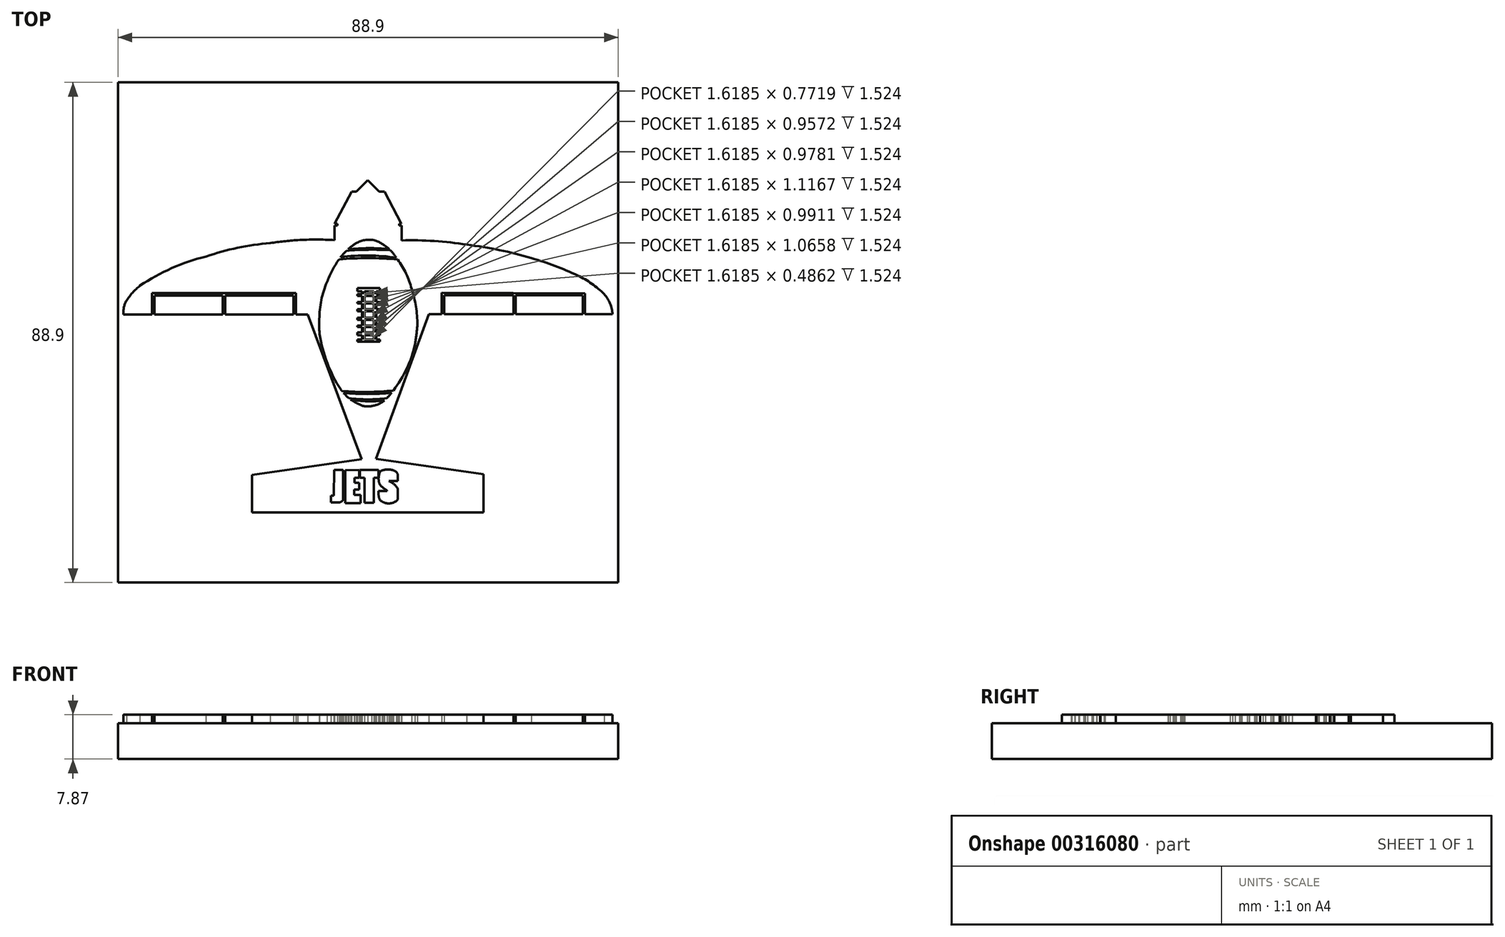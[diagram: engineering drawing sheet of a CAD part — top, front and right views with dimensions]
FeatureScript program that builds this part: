
annotation { "Feature Type Name" : "Feature", "Feature Type Description" : "" }
export const myFeature = defineFeature(function(context is Context, id is Id, definition is map)
    precondition{}
    {
        {
            var Q0;
            Q0=qCreatedBy(makeId("Top.planeOp"),FACE);
            var sketch = newSketch(context, id + "F0", { "sketchPlane" : qUnion([Q0])});
            skLineSegment(sketch, "E0.bottom", {"start": v(0, 0) * mm, "end": v(88.9, 0) * mm});
            skLineSegment(sketch, "E0.top", {"start": v(0, 88.9) * mm, "end": v(88.9, 88.9) * mm});
            skLineSegment(sketch, "E0.left", {"start": v(0, 0) * mm, "end": v(0, 88.9) * mm});
            skLineSegment(sketch, "E0.right", {"start": v(88.9, 0) * mm, "end": v(88.9, 88.9) * mm});
            skSolve(sketch);
        }
        {
            var Q0;
            Q0=makeQuery(id+"F0.imprint","IMPRINT",FACE,{"disambiguationData":[TD([[makeQuery(id+"F0.imprint","IMPRINT",EDGE,{"derivedFrom":sQuery(id+"F0.wireOp",EDGE,"E0.bottom")}),1.0]])]});
            extrude(context, id + "F1", {"entities" : qUnion([Q0]), "depth" : 6.35 * mm});
        }
        {
            var Q0;
            Q0=makeQuery(id+"F1.opExtrude","CAP_FACE",FACE,{"disambiguationData":[OSD([sQuery(id+"F0.wireOp",EDGE,"E0.bottom"),sQuery(id+"F0.wireOp",EDGE,"E0.top"),sQuery(id+"F0.wireOp",EDGE,"E0.left"),sQuery(id+"F0.wireOp",EDGE,"E0.right")])],"isStart":false});
            var sketch = newSketch(context, id + "F2", { "sketchPlane" : qUnion([Q0])});
            skLineSegment(sketch, "E1", {"start": v(43.29, 21.93) * mm, "end": v(23.83, 19.13) * mm});
            skLineSegment(sketch, "E2", {"start": v(23.83, 19.13) * mm, "end": v(23.83, 12.44) * mm});
            skLineSegment(sketch, "E3", {"start": v(23.83, 12.44) * mm, "end": v(64.97, 12.44) * mm});
            skLineSegment(sketch, "E4", {"start": v(64.97, 12.44) * mm, "end": v(64.97, 19.23) * mm});
            skLineSegment(sketch, "E5", {"start": v(64.97, 19.23) * mm, "end": v(45.85, 22) * mm});
            skLineSegment(sketch, "E6", {"start": v(45.85, 22) * mm, "end": v(55.28, 47.7) * mm});
            skLineSegment(sketch, "E7", {"start": v(55.28, 47.7) * mm, "end": v(87.89, 47.7) * mm});
            skLineSegment(sketch, "E8", {"start": v(43.29, 21.93) * mm, "end": v(33.7, 47.66) * mm});
            skLineSegment(sketch, "E9", {"start": v(33.7, 47.66) * mm, "end": v(0.98, 47.66) * mm});
            skArc(sketch, "E10", {"start": v(1.51, 50.1) * mm, "mid": v(1.05, 48.92) * mm, "end": v(0.98, 47.66) * mm});
            skArc(sketch, "E11", {"start": v(3.9, 52.77) * mm, "mid": v(2.6, 51.54) * mm, "end": v(1.51, 50.1) * mm});
            skArc(sketch, "E12", {"start": v(15.62, 57.96) * mm, "mid": v(9.54, 55.87) * mm, "end": v(3.9, 52.77) * mm});
            skArc(sketch, "E13", {"start": v(27.06, 60.35) * mm, "mid": v(21.27, 59.5) * mm, "end": v(15.62, 57.96) * mm});
            skArc(sketch, "E14", {"start": v(31.92, 60.89) * mm, "mid": v(29.49, 60.65) * mm, "end": v(27.06, 60.35) * mm});
            skArc(sketch, "E15", {"start": v(38.5, 60.89) * mm, "mid": v(35.22, 60.96) * mm, "end": v(31.92, 60.89) * mm});
            skLineSegment(sketch, "E16", {"start": v(38.5, 60.89) * mm, "end": v(38.5, 63.8) * mm});
            skLineSegment(sketch, "E17", {"start": v(38.5, 63.8) * mm, "end": v(41.53, 69.51) * mm});
            skLineSegment(sketch, "E18", {"start": v(41.53, 69.51) * mm, "end": v(42.36, 69.51) * mm});
            skLineSegment(sketch, "E19", {"start": v(42.36, 69.51) * mm, "end": v(44.4, 71.55) * mm});
            skLineSegment(sketch, "E20", {"start": v(44.4, 71.55) * mm, "end": v(46.45, 69.51) * mm});
            skLineSegment(sketch, "E21", {"start": v(46.45, 69.51) * mm, "end": v(47.36, 69.51) * mm});
            skLineSegment(sketch, "E22", {"start": v(47.36, 69.51) * mm, "end": v(50.4, 63.73) * mm});
            skLineSegment(sketch, "E23", {"start": v(50.4, 63.73) * mm, "end": v(50.4, 60.81) * mm});
            skArc(sketch, "E24", {"start": v(62.01, 60.06) * mm, "mid": v(56.22, 60.7) * mm, "end": v(50.4, 60.81) * mm});
            skArc(sketch, "E25", {"start": v(73.5, 57.67) * mm, "mid": v(67.8, 59.1) * mm, "end": v(62.01, 60.06) * mm});
            skArc(sketch, "E26", {"start": v(81.72, 54.57) * mm, "mid": v(77.67, 56.3) * mm, "end": v(73.5, 57.67) * mm});
            skArc(sketch, "E27", {"start": v(86.42, 51.26) * mm, "mid": v(84.22, 53.12) * mm, "end": v(81.72, 54.57) * mm});
            skArc(sketch, "E28", {"start": v(87.89, 47.7) * mm, "mid": v(87.47, 49.6) * mm, "end": v(86.42, 51.26) * mm});
            skLineSegment(sketch, "E29", {"start": v(6.04, 47.66) * mm, "end": v(6.04, 51.44) * mm});
            skLineSegment(sketch, "E30", {"start": v(6.04, 51.44) * mm, "end": v(31.62, 51.44) * mm});
            skLineSegment(sketch, "E31", {"start": v(31.62, 51.44) * mm, "end": v(31.62, 47.66) * mm});
            skLineSegment(sketch, "E32", {"start": v(31.19, 47.66) * mm, "end": v(31.19, 51.44) * mm});
            skLineSegment(sketch, "E33", {"start": v(19.05, 51.44) * mm, "end": v(19.05, 47.66) * mm});
            skLineSegment(sketch, "E34", {"start": v(18.64, 51.44) * mm, "end": v(18.64, 47.66) * mm});
            skLineSegment(sketch, "E35", {"start": v(6.47, 51.44) * mm, "end": v(6.47, 47.66) * mm});
            skLineSegment(sketch, "E36", {"start": v(57.57, 47.7) * mm, "end": v(57.57, 51.55) * mm});
            skLineSegment(sketch, "E37", {"start": v(57.57, 51.55) * mm, "end": v(82.99, 51.42) * mm});
            skLineSegment(sketch, "E38", {"start": v(82.99, 51.42) * mm, "end": v(82.99, 47.7) * mm});
            skLineSegment(sketch, "E39", {"start": v(70.28, 51.49) * mm, "end": v(70.28, 48.09) * mm});
            skLineSegment(sketch, "E40", {"start": v(70.66, 51.48) * mm, "end": v(70.66, 48.09) * mm});
            skArc(sketch, "E41", {"start": v(35.79, 46.83) * mm, "mid": v(35.76, 45.5) * mm, "end": v(35.85, 44.18) * mm});
            skArc(sketch, "E42", {"start": v(37.16, 53.42) * mm, "mid": v(36.14, 50.2) * mm, "end": v(35.79, 46.83) * mm});
            skArc(sketch, "E43", {"start": v(39.56, 57.83) * mm, "mid": v(38.21, 55.7) * mm, "end": v(37.16, 53.42) * mm});
            skArc(sketch, "E44", {"start": v(42.46, 60.4) * mm, "mid": v(40.9, 59.24) * mm, "end": v(39.56, 57.83) * mm});
            skArc(sketch, "E45", {"start": v(45.73, 60.82) * mm, "mid": v(44.06, 60.9) * mm, "end": v(42.46, 60.4) * mm});
            skArc(sketch, "E46", {"start": v(49.5, 57.73) * mm, "mid": v(47.85, 59.56) * mm, "end": v(45.73, 60.82) * mm});
            skArc(sketch, "E47", {"start": v(52.2, 52.2) * mm, "mid": v(51.12, 55.09) * mm, "end": v(49.5, 57.73) * mm});
            skArc(sketch, "E48", {"start": v(53.22, 45.8) * mm, "mid": v(52.96, 49.03) * mm, "end": v(52.2, 52.2) * mm});
            skArc(sketch, "E49", {"start": v(52.8, 42.33) * mm, "mid": v(53.04, 44.06) * mm, "end": v(53.22, 45.8) * mm});
            skArc(sketch, "E50", {"start": v(48.2, 59.26) * mm, "mid": v(44.55, 59.44) * mm, "end": v(40.9, 59.24) * mm});
            skArc(sketch, "E51", {"start": v(48.39, 59.08) * mm, "mid": v(44.5, 59.17) * mm, "end": v(40.6, 58.98) * mm});
            skArc(sketch, "E52", {"start": v(49.5, 57.73) * mm, "mid": v(44.53, 58.14) * mm, "end": v(39.56, 57.83) * mm});
            skArc(sketch, "E53", {"start": v(49.71, 57.43) * mm, "mid": v(44.5, 57.67) * mm, "end": v(39.28, 57.45) * mm});
            skArc(sketch, "E54", {"start": v(35.85, 44.18) * mm, "mid": v(37.2, 39.04) * mm, "end": v(39.6, 34.3) * mm});
            skArc(sketch, "E55", {"start": v(39.6, 34.3) * mm, "mid": v(41.06, 32.78) * mm, "end": v(42.87, 31.7) * mm});
            skArc(sketch, "E56", {"start": v(42.87, 31.7) * mm, "mid": v(43.95, 31.33) * mm, "end": v(45.09, 31.37) * mm});
            skArc(sketch, "E57", {"start": v(45.09, 31.37) * mm, "mid": v(46.46, 31.8) * mm, "end": v(47.65, 32.61) * mm});
            skArc(sketch, "E58", {"start": v(47.65, 32.61) * mm, "mid": v(50.87, 37.13) * mm, "end": v(52.8, 42.33) * mm});
            skArc(sketch, "E59", {"start": v(39.8, 34.06) * mm, "mid": v(44.38, 33.88) * mm, "end": v(48.96, 34.15) * mm});
            skArc(sketch, "E60", {"start": v(40.09, 33.7) * mm, "mid": v(44.35, 33.52) * mm, "end": v(48.62, 33.72) * mm});
            skArc(sketch, "E61", {"start": v(41.06, 32.78) * mm, "mid": v(44.44, 32.56) * mm, "end": v(47.81, 32.78) * mm});
            skPoint(sketch, "E61.endSnap0", {"position": v(41.06, 32.78) * mm});
            skArc(sketch, "E62", {"start": v(41.35, 32.56) * mm, "mid": v(44.35, 32.22) * mm, "end": v(47.37, 32.37) * mm});
            skLineSegment(sketch, "E63", {"start": v(38.5, 63.8) * mm, "end": v(50.36, 63.8) * mm});
            skLineSegment(sketch, "E64", {"start": v(40.04, 19.93) * mm, "end": v(40.04, 14.74) * mm});
            skArc(sketch, "E65", {"start": v(39.33, 14.24) * mm, "mid": v(39.75, 14.4) * mm, "end": v(40.04, 14.74) * mm});
            skLineSegment(sketch, "E66", {"start": v(39.33, 14.24) * mm, "end": v(37.84, 14.24) * mm});
            skLineSegment(sketch, "E67", {"start": v(37.84, 14.24) * mm, "end": v(37.84, 15.43) * mm});
            skLineSegment(sketch, "E68", {"start": v(37.84, 15.43) * mm, "end": v(38.39, 15.43) * mm});
            skLineSegment(sketch, "E69", {"start": v(38.39, 15.43) * mm, "end": v(38.46, 20.02) * mm});
            skLineSegment(sketch, "E70", {"start": v(38.46, 20.02) * mm, "end": v(40.04, 20.02) * mm});
            skLineSegment(sketch, "E71", {"start": v(40.04, 20.02) * mm, "end": v(40.04, 19.93) * mm});
            skLineSegment(sketch, "E72", {"start": v(40.36, 19.97) * mm, "end": v(40.36, 14.14) * mm});
            skLineSegment(sketch, "E73", {"start": v(40.36, 14.14) * mm, "end": v(43.13, 14.14) * mm});
            skLineSegment(sketch, "E74", {"start": v(43.13, 14.14) * mm, "end": v(43.13, 15.57) * mm});
            skLineSegment(sketch, "E75", {"start": v(43.13, 15.57) * mm, "end": v(42, 15.57) * mm});
            skLineSegment(sketch, "E76", {"start": v(42, 15.57) * mm, "end": v(42, 16.53) * mm});
            skLineSegment(sketch, "E77", {"start": v(42, 16.53) * mm, "end": v(42.86, 16.53) * mm});
            skLineSegment(sketch, "E78", {"start": v(42.86, 16.53) * mm, "end": v(42.86, 17.77) * mm});
            skLineSegment(sketch, "E79", {"start": v(42.86, 17.77) * mm, "end": v(42.04, 17.77) * mm});
            skLineSegment(sketch, "E80", {"start": v(42.04, 17.77) * mm, "end": v(42.04, 18.63) * mm});
            skLineSegment(sketch, "E81", {"start": v(42.04, 18.63) * mm, "end": v(42.86, 18.63) * mm});
            skLineSegment(sketch, "E82", {"start": v(42.86, 18.63) * mm, "end": v(42.86, 20.02) * mm});
            skLineSegment(sketch, "E83", {"start": v(42.86, 20.02) * mm, "end": v(40.36, 19.97) * mm});
            skLineSegment(sketch, "E84", {"start": v(43, 20) * mm, "end": v(43, 18.61) * mm});
            skLineSegment(sketch, "E85", {"start": v(43, 18.61) * mm, "end": v(43.83, 18.61) * mm});
            skLineSegment(sketch, "E86", {"start": v(43.83, 18.61) * mm, "end": v(43.83, 14.16) * mm});
            skLineSegment(sketch, "E87", {"start": v(43.83, 14.16) * mm, "end": v(45.5, 14.16) * mm});
            skLineSegment(sketch, "E88", {"start": v(45.5, 14.16) * mm, "end": v(45.5, 18.62) * mm});
            skLineSegment(sketch, "E89", {"start": v(45.5, 18.62) * mm, "end": v(46.29, 18.62) * mm});
            skLineSegment(sketch, "E90", {"start": v(46.29, 18.62) * mm, "end": v(46.29, 20.02) * mm});
            skLineSegment(sketch, "E91", {"start": v(46.29, 20.02) * mm, "end": v(43, 20) * mm});
            skLineSegment(sketch, "E92", {"start": v(48.13, 18.82) * mm, "end": v(48.13, 18.05) * mm});
            skLineSegment(sketch, "E93", {"start": v(48.13, 18.05) * mm, "end": v(49.71, 18.05) * mm});
            skLineSegment(sketch, "E94", {"start": v(49.71, 18.05) * mm, "end": v(49.71, 19.26) * mm});
            skArc(sketch, "E95", {"start": v(49.71, 19.26) * mm, "mid": v(49.4, 19.71) * mm, "end": v(48.9, 19.96) * mm});
            skArc(sketch, "E96", {"start": v(48.9, 19.96) * mm, "mid": v(48.04, 20.1) * mm, "end": v(47.17, 20) * mm});
            skArc(sketch, "E97", {"start": v(47.17, 20) * mm, "mid": v(46.72, 19.82) * mm, "end": v(46.48, 19.41) * mm});
            skArc(sketch, "E98", {"start": v(46.48, 19.41) * mm, "mid": v(46.33, 18.64) * mm, "end": v(46.39, 17.85) * mm});
            skArc(sketch, "E99", {"start": v(46.39, 17.85) * mm, "mid": v(46.58, 17.38) * mm, "end": v(46.94, 17.01) * mm});
            skArc(sketch, "E100", {"start": v(46.94, 17.01) * mm, "mid": v(47.62, 16.49) * mm, "end": v(48.3, 15.97) * mm});
            skLineSegment(sketch, "E101", {"start": v(48.3, 15.97) * mm, "end": v(48.3, 15.3) * mm});
            skArc(sketch, "E102", {"start": v(47.9, 15.3) * mm, "mid": v(48.1, 15.1) * mm, "end": v(48.3, 15.3) * mm});
            skLineSegment(sketch, "E103", {"start": v(47.9, 15.3) * mm, "end": v(47.85, 16.3) * mm});
            skLineSegment(sketch, "E104", {"start": v(47.85, 16.3) * mm, "end": v(46.28, 16.3) * mm});
            skArc(sketch, "E105", {"start": v(46.28, 16.3) * mm, "mid": v(46.32, 15.52) * mm, "end": v(46.5, 14.76) * mm});
            skArc(sketch, "E106", {"start": v(46.5, 14.76) * mm, "mid": v(48.12, 14.06) * mm, "end": v(49.74, 14.76) * mm});
            skLineSegment(sketch, "E107", {"start": v(49.74, 14.76) * mm, "end": v(49.74, 16.66) * mm});
            skArc(sketch, "E108", {"start": v(49.74, 16.66) * mm, "mid": v(49.06, 17.5) * mm, "end": v(48.13, 18.05) * mm});
            skArc(sketch, "E109", {"start": v(48.13, 18.82) * mm, "mid": v(47.86, 19) * mm, "end": v(47.79, 18.68) * mm});
            skLineSegment(sketch, "E110", {"start": v(47.79, 18.68) * mm, "end": v(47.79, 18.32) * mm});
            skArc(sketch, "E111", {"start": v(47.79, 18.32) * mm, "mid": v(47.9, 18.1) * mm, "end": v(48.13, 18.05) * mm});
            skArc(sketch, "E112", {"start": v(40.12, 61.25) * mm, "mid": v(38.87, 60.47) * mm, "end": v(38.14, 59.18) * mm});
            skArc(sketch, "E113", {"start": v(44.09, 62.2) * mm, "mid": v(42.04, 61.99) * mm, "end": v(40.12, 61.25) * mm});
            skArc(sketch, "E114", {"start": v(47.7, 61.6) * mm, "mid": v(45.92, 62.06) * mm, "end": v(44.09, 62.2) * mm});
            skArc(sketch, "E115", {"start": v(50.87, 59.07) * mm, "mid": v(49.64, 60.77) * mm, "end": v(47.7, 61.6) * mm});
            skLineSegment(sketch, "E116", {"start": v(50.87, 59.07) * mm, "end": v(51.2, 59.07) * mm});
            skLineSegment(sketch, "E117", {"start": v(38.14, 59.18) * mm, "end": v(37.7, 59.18) * mm});
            skArc(sketch, "E118", {"start": v(38.5, 60.63) * mm, "mid": v(38, 59.96) * mm, "end": v(37.7, 59.18) * mm});
            skArc(sketch, "E119", {"start": v(49.9, 60.89) * mm, "mid": v(44.45, 62.53) * mm, "end": v(38.99, 60.89) * mm});
            skLineSegment(sketch, "E120.bottom", {"start": v(42.52, 52.32) * mm, "end": v(46.53, 52.32) * mm});
            skLineSegment(sketch, "E120.top", {"start": v(42.52, 42.82) * mm, "end": v(46.53, 42.82) * mm});
            skLineSegment(sketch, "E120.left", {"start": v(42.52, 52.32) * mm, "end": v(42.52, 42.82) * mm});
            skLineSegment(sketch, "E120.right", {"start": v(46.53, 52.32) * mm, "end": v(46.53, 42.82) * mm});
            skLineSegment(sketch, "E121", {"start": v(42.52, 51.75) * mm, "end": v(43.35, 51.75) * mm});
            skLineSegment(sketch, "E122", {"start": v(42.52, 50.96) * mm, "end": v(43.35, 50.96) * mm});
            skLineSegment(sketch, "E123", {"start": v(42.52, 51.26) * mm, "end": v(43.35, 51.26) * mm});
            skLineSegment(sketch, "E124", {"start": v(42.52, 49.9) * mm, "end": v(43.35, 49.9) * mm});
            skLineSegment(sketch, "E125", {"start": v(42.52, 49.6) * mm, "end": v(43.35, 49.6) * mm});
            skLineSegment(sketch, "E126", {"start": v(42.52, 48.6) * mm, "end": v(43.35, 48.6) * mm});
            skLineSegment(sketch, "E127", {"start": v(42.52, 48.2) * mm, "end": v(43.35, 48.2) * mm});
            skLineSegment(sketch, "E128", {"start": v(42.52, 47.08) * mm, "end": v(43.35, 47.08) * mm});
            skLineSegment(sketch, "E129", {"start": v(42.52, 46.67) * mm, "end": v(43.35, 46.67) * mm});
            skLineSegment(sketch, "E130", {"start": v(42.52, 45.7) * mm, "end": v(43.35, 45.7) * mm});
            skLineSegment(sketch, "E131", {"start": v(42.52, 45.42) * mm, "end": v(43.35, 45.42) * mm});
            skLineSegment(sketch, "E132", {"start": v(42.52, 44.46) * mm, "end": v(43.35, 44.46) * mm});
            skLineSegment(sketch, "E133", {"start": v(42.52, 43.99) * mm, "end": v(43.35, 43.99) * mm});
            skLineSegment(sketch, "E134", {"start": v(42.52, 43.22) * mm, "end": v(43.35, 43.22) * mm});
            skLineSegment(sketch, "E135", {"start": v(43.35, 51.75) * mm, "end": v(43.35, 43.22) * mm});
            skLineSegment(sketch, "E136", {"start": v(43.85, 51.75) * mm, "end": v(43.85, 43.22) * mm});
            skLineSegment(sketch, "E137", {"start": v(45.47, 51.75) * mm, "end": v(45.47, 43.22) * mm});
            skLineSegment(sketch, "E138", {"start": v(45.89, 51.75) * mm, "end": v(45.89, 43.22) * mm});
            skLineSegment(sketch, "E139.trimOffspring", {"start": v(43.85, 50.96) * mm, "end": v(45.47, 50.96) * mm});
            skLineSegment(sketch, "E140.trimOffspring", {"start": v(43.85, 51.26) * mm, "end": v(45.47, 51.26) * mm});
            skLineSegment(sketch, "E141.trimOffspring", {"start": v(43.85, 49.9) * mm, "end": v(45.47, 49.9) * mm});
            skLineSegment(sketch, "E142.trimOffspring", {"start": v(43.85, 49.6) * mm, "end": v(45.47, 49.6) * mm});
            skLineSegment(sketch, "E143.trimOffspring", {"start": v(43.85, 48.6) * mm, "end": v(45.47, 48.6) * mm});
            skLineSegment(sketch, "E144.trimOffspring", {"start": v(43.85, 48.2) * mm, "end": v(45.47, 48.2) * mm});
            skLineSegment(sketch, "E145.trimOffspring", {"start": v(43.85, 47.08) * mm, "end": v(45.47, 47.08) * mm});
            skLineSegment(sketch, "E146.trimOffspring", {"start": v(43.85, 46.67) * mm, "end": v(45.47, 46.67) * mm});
            skLineSegment(sketch, "E147.trimOffspring", {"start": v(43.85, 45.7) * mm, "end": v(45.47, 45.7) * mm});
            skLineSegment(sketch, "E148.trimOffspring", {"start": v(43.85, 45.42) * mm, "end": v(45.47, 45.42) * mm});
            skLineSegment(sketch, "E149.trimOffspring", {"start": v(43.85, 44.46) * mm, "end": v(45.47, 44.46) * mm});
            skLineSegment(sketch, "E150.trimOffspring", {"start": v(43.85, 43.99) * mm, "end": v(45.47, 43.99) * mm});
            skLineSegment(sketch, "E151.trimOffspring", {"start": v(43.85, 43.22) * mm, "end": v(45.47, 43.22) * mm});
            skLineSegment(sketch, "E152.trimOffspring", {"start": v(45.89, 43.22) * mm, "end": v(46.53, 43.22) * mm});
            skLineSegment(sketch, "E153.trimOffspring", {"start": v(45.89, 43.99) * mm, "end": v(46.53, 43.99) * mm});
            skLineSegment(sketch, "E154.trimOffspring", {"start": v(45.89, 44.46) * mm, "end": v(46.53, 44.46) * mm});
            skLineSegment(sketch, "E155.trimOffspring", {"start": v(45.89, 45.42) * mm, "end": v(46.53, 45.42) * mm});
            skLineSegment(sketch, "E156.trimOffspring", {"start": v(45.89, 45.7) * mm, "end": v(46.53, 45.7) * mm});
            skLineSegment(sketch, "E157.trimOffspring", {"start": v(45.89, 46.67) * mm, "end": v(46.53, 46.67) * mm});
            skLineSegment(sketch, "E158.trimOffspring", {"start": v(45.89, 47.08) * mm, "end": v(46.53, 47.08) * mm});
            skLineSegment(sketch, "E159.trimOffspring", {"start": v(45.89, 48.2) * mm, "end": v(46.53, 48.2) * mm});
            skLineSegment(sketch, "E160.trimOffspring", {"start": v(45.89, 48.6) * mm, "end": v(46.53, 48.6) * mm});
            skLineSegment(sketch, "E161.trimOffspring", {"start": v(45.89, 49.6) * mm, "end": v(46.53, 49.6) * mm});
            skLineSegment(sketch, "E162.trimOffspring", {"start": v(45.89, 49.9) * mm, "end": v(46.53, 49.9) * mm});
            skLineSegment(sketch, "E163.trimOffspring", {"start": v(45.89, 50.96) * mm, "end": v(46.53, 50.96) * mm});
            skLineSegment(sketch, "E164.trimOffspring", {"start": v(45.89, 51.26) * mm, "end": v(46.53, 51.26) * mm});
            skLineSegment(sketch, "E165.trimOffspring", {"start": v(43.85, 51.75) * mm, "end": v(45.47, 51.75) * mm});
            skLineSegment(sketch, "E166.trimOffspring", {"start": v(45.89, 51.75) * mm, "end": v(46.53, 51.75) * mm});
            skLineSegment(sketch, "E167", {"start": v(57.97, 48.09) * mm, "end": v(70.28, 48.09) * mm});
            skLineSegment(sketch, "E168", {"start": v(70.66, 48.09) * mm, "end": v(82.62, 48.09) * mm});
            skLineSegment(sketch, "E169", {"start": v(70.28, 48.09) * mm, "end": v(70.66, 48.09) * mm});
            skPoint(sketch, "E170.orphan", {"position": v(70.28, 47.7) * mm});
            skLineSegment(sketch, "E171", {"start": v(6.47, 48.05) * mm, "end": v(18.64, 48.05) * mm});
            skPoint(sketch, "E172.orphan", {"position": v(6.04, 48.05) * mm});
            skLineSegment(sketch, "E173.trimOffspring", {"start": v(19.05, 48.05) * mm, "end": v(31.19, 48.05) * mm});
            skLineSegment(sketch, "E174", {"start": v(18.64, 48.05) * mm, "end": v(19.05, 48.05) * mm});
            skLineSegment(sketch, "E175", {"start": v(70.66, 48.09) * mm, "end": v(70.66, 47.7) * mm});
            skLineSegment(sketch, "E176", {"start": v(70.28, 48.09) * mm, "end": v(70.28, 47.7) * mm});
            skPoint(sketch, "E177.orphan", {"position": v(70.67, 48.09) * mm});
            skPoint(sketch, "E178.end.orphan", {"position": v(70.66, 51.4) * mm});
            skLineSegment(sketch, "E179", {"start": v(6.47, 51) * mm, "end": v(18.64, 51) * mm});
            skLineSegment(sketch, "E180", {"start": v(19.05, 51.02) * mm, "end": v(31.19, 51.02) * mm});
            skLineSegment(sketch, "E181", {"start": v(57.97, 51.05) * mm, "end": v(70.28, 51.05) * mm});
            skLineSegment(sketch, "E182", {"start": v(70.66, 51.05) * mm, "end": v(82.62, 51) * mm});
            skLineSegment(sketch, "E183", {"start": v(57.97, 51.55) * mm, "end": v(57.97, 47.7) * mm});
            skLineSegment(sketch, "E184", {"start": v(82.62, 51.42) * mm, "end": v(82.62, 47.7) * mm});
            skLineSegment(sketch, "E185", {"start": v(38.5, 63.43) * mm, "end": v(50.4, 63.43) * mm});
            skLineSegment(sketch, "E186", {"start": v(38.98, 63.8) * mm, "end": v(38.98, 63.43) * mm});
            skLineSegment(sketch, "E187", {"start": v(49.98, 63.8) * mm, "end": v(49.98, 63.43) * mm});
            skSolve(sketch);
        }
        {
            var Q0;
            {var subQ0=sQuery(id+"F2.wireOp",EDGE,"E186");Q0=makeQuery(id+"F2.imprint","IMPRINT",FACE,{"disambiguationData":[TD([[makeQuery(id+"F2.imprint","IMPRINT",EDGE,{"derivedFrom":subQ0}),1.0]])]});}
            var Q1;
            {var subQ0=sQuery(id+"F2.wireOp",EDGE,"E171");Q1=makeQuery(id+"F2.imprint","IMPRINT",FACE,{"disambiguationData":[TD([[makeQuery(id+"F2.imprint","IMPRINT",EDGE,{"derivedFrom":subQ0}),1.0]])]});}
            var Q2;
            {var subQ0=sQuery(id+"F2.wireOp",EDGE,"E173.trimOffspring");Q2=makeQuery(id+"F2.imprint","IMPRINT",FACE,{"disambiguationData":[TD([[makeQuery(id+"F2.imprint","IMPRINT",EDGE,{"derivedFrom":subQ0}),1.0]])]});}
            var Q3;
            {var subQ0=sQuery(id+"F2.wireOp",EDGE,"E59");Q3=makeQuery(id+"F2.imprint","IMPRINT",FACE,{"disambiguationData":[TD([[makeQuery(id+"F2.imprint","IMPRINT",EDGE,{"derivedFrom":subQ0}),-1.0]])]});}
            var Q4;
            {var subQ0=sQuery(id+"F2.wireOp",EDGE,"E61");Q4=makeQuery(id+"F2.imprint","IMPRINT",FACE,{"disambiguationData":[TD([[makeQuery(id+"F2.imprint","IMPRINT",EDGE,{"derivedFrom":subQ0}),-1.0]])]});}
            var Q5;
            {var subQ1=sQuery(id+"F2.wireOp",EDGE,"E17");Q5=makeQuery(id+"F2.imprint","IMPRINT",FACE,{"disambiguationData":[TD([[makeQuery(id+"F2.imprint","IMPRINT",EDGE,{"derivedFrom":subQ1}),-1.0]])]});}
            var Q6;
            Q6=makeQuery(id+"F2.imprint","IMPRINT",FACE,{"disambiguationData":[TD([[makeQuery(id+"F2.imprint","IMPRINT",EDGE,{"derivedFrom":sQuery(id+"F2.wireOp",EDGE,"E1")}),1.0]])]});
            var Q7;
            {var subQ4=sQuery(id+"F2.wireOp",EDGE,"E167");Q7=makeQuery(id+"F2.imprint","IMPRINT",FACE,{"disambiguationData":[TD([[makeQuery(id+"F2.imprint","IMPRINT",EDGE,{"derivedFrom":subQ4}),-1.0]])]});}
            var Q8;
            {var subQ0=sQuery(id+"F2.wireOp",EDGE,"E168");Q8=makeQuery(id+"F2.imprint","IMPRINT",FACE,{"disambiguationData":[TD([[makeQuery(id+"F2.imprint","IMPRINT",EDGE,{"derivedFrom":subQ0}),1.0]])]});}
            var Q9;
            {var subQ0=sQuery(id+"F2.wireOp",EDGE,"E167");Q9=makeQuery(id+"F2.imprint","IMPRINT",FACE,{"disambiguationData":[TD([[makeQuery(id+"F2.imprint","IMPRINT",EDGE,{"derivedFrom":subQ0}),1.0]])]});}
            var Q10;
            {var subQ4=sQuery(id+"F2.wireOp",EDGE,"E168");Q10=makeQuery(id+"F2.imprint","IMPRINT",FACE,{"disambiguationData":[TD([[makeQuery(id+"F2.imprint","IMPRINT",EDGE,{"derivedFrom":subQ4}),-1.0]])]});}
            var Q11;
            {var subQ5=sQuery(id+"F2.wireOp",EDGE,"E173.trimOffspring");Q11=makeQuery(id+"F2.imprint","IMPRINT",FACE,{"disambiguationData":[TD([[makeQuery(id+"F2.imprint","IMPRINT",EDGE,{"derivedFrom":subQ5}),-1.0]])]});}
            var Q12;
            {var subQ5=sQuery(id+"F2.wireOp",EDGE,"E171");Q12=makeQuery(id+"F2.imprint","IMPRINT",FACE,{"disambiguationData":[TD([[makeQuery(id+"F2.imprint","IMPRINT",EDGE,{"derivedFrom":subQ5}),-1.0]])]});}
            var Q13;
            {var subQ0=sQuery(id+"F2.wireOp",EDGE,"E50");Q13=makeQuery(id+"F2.imprint","IMPRINT",FACE,{"disambiguationData":[TD([[makeQuery(id+"F2.imprint","IMPRINT",EDGE,{"derivedFrom":subQ0}),1.0]])]});}
            var Q14;
            {var subQ48=sQuery(id+"F2.wireOp",EDGE,"E120.bottom");Q14=makeQuery(id+"F2.imprint","IMPRINT",FACE,{"disambiguationData":[TD([[makeQuery(id+"F2.imprint","IMPRINT",EDGE,{"derivedFrom":subQ48}),-1.0]])]});}
            var Q15;
            {var subQ0=sQuery(id+"F2.wireOp",EDGE,"E52");Q15=makeQuery(id+"F2.imprint","IMPRINT",FACE,{"disambiguationData":[TD([[makeQuery(id+"F2.imprint","IMPRINT",EDGE,{"derivedFrom":subQ0}),1.0]])]});}
            var Q16;
            {var subQ0=sQuery(id+"F2.wireOp",EDGE,"E159.trimOffspring");Q16=makeQuery(id+"F2.imprint","IMPRINT",FACE,{"disambiguationData":[TD([[makeQuery(id+"F2.imprint","IMPRINT",EDGE,{"derivedFrom":subQ0}),1.0]])]});}
            var Q17;
            {var subQ0=sQuery(id+"F2.wireOp",EDGE,"E143.trimOffspring");Q17=makeQuery(id+"F2.imprint","IMPRINT",FACE,{"disambiguationData":[TD([[makeQuery(id+"F2.imprint","IMPRINT",EDGE,{"derivedFrom":subQ0}),-1.0]])]});}
            var Q18;
            {var subQ0=sQuery(id+"F2.wireOp",EDGE,"E126");Q18=makeQuery(id+"F2.imprint","IMPRINT",FACE,{"disambiguationData":[TD([[makeQuery(id+"F2.imprint","IMPRINT",EDGE,{"derivedFrom":subQ0}),-1.0]])]});}
            var Q19;
            {var subQ0=sQuery(id+"F2.wireOp",EDGE,"E124");Q19=makeQuery(id+"F2.imprint","IMPRINT",FACE,{"disambiguationData":[TD([[makeQuery(id+"F2.imprint","IMPRINT",EDGE,{"derivedFrom":subQ0}),-1.0]])]});}
            var Q20;
            {var subQ0=sQuery(id+"F2.wireOp",EDGE,"E141.trimOffspring");Q20=makeQuery(id+"F2.imprint","IMPRINT",FACE,{"disambiguationData":[TD([[makeQuery(id+"F2.imprint","IMPRINT",EDGE,{"derivedFrom":subQ0}),-1.0]])]});}
            var Q21;
            {var subQ0=sQuery(id+"F2.wireOp",EDGE,"E161.trimOffspring");Q21=makeQuery(id+"F2.imprint","IMPRINT",FACE,{"disambiguationData":[TD([[makeQuery(id+"F2.imprint","IMPRINT",EDGE,{"derivedFrom":subQ0}),1.0]])]});}
            var Q22;
            {var subQ0=sQuery(id+"F2.wireOp",EDGE,"E163.trimOffspring");Q22=makeQuery(id+"F2.imprint","IMPRINT",FACE,{"disambiguationData":[TD([[makeQuery(id+"F2.imprint","IMPRINT",EDGE,{"derivedFrom":subQ0}),1.0]])]});}
            var Q23;
            {var subQ0=sQuery(id+"F2.wireOp",EDGE,"E139.trimOffspring");Q23=makeQuery(id+"F2.imprint","IMPRINT",FACE,{"disambiguationData":[TD([[makeQuery(id+"F2.imprint","IMPRINT",EDGE,{"derivedFrom":subQ0}),1.0]])]});}
            var Q24;
            {var subQ0=sQuery(id+"F2.wireOp",EDGE,"E122");Q24=makeQuery(id+"F2.imprint","IMPRINT",FACE,{"disambiguationData":[TD([[makeQuery(id+"F2.imprint","IMPRINT",EDGE,{"derivedFrom":subQ0}),1.0]])]});}
            var Q25;
            {var subQ0=sQuery(id+"F2.wireOp",EDGE,"E128");Q25=makeQuery(id+"F2.imprint","IMPRINT",FACE,{"disambiguationData":[TD([[makeQuery(id+"F2.imprint","IMPRINT",EDGE,{"derivedFrom":subQ0}),-1.0]])]});}
            var Q26;
            {var subQ0=sQuery(id+"F2.wireOp",EDGE,"E145.trimOffspring");Q26=makeQuery(id+"F2.imprint","IMPRINT",FACE,{"disambiguationData":[TD([[makeQuery(id+"F2.imprint","IMPRINT",EDGE,{"derivedFrom":subQ0}),-1.0]])]});}
            var Q27;
            {var subQ0=sQuery(id+"F2.wireOp",EDGE,"E157.trimOffspring");Q27=makeQuery(id+"F2.imprint","IMPRINT",FACE,{"disambiguationData":[TD([[makeQuery(id+"F2.imprint","IMPRINT",EDGE,{"derivedFrom":subQ0}),1.0]])]});}
            var Q28;
            {var subQ0=sQuery(id+"F2.wireOp",EDGE,"E130");Q28=makeQuery(id+"F2.imprint","IMPRINT",FACE,{"disambiguationData":[TD([[makeQuery(id+"F2.imprint","IMPRINT",EDGE,{"derivedFrom":subQ0}),-1.0]])]});}
            var Q29;
            {var subQ0=sQuery(id+"F2.wireOp",EDGE,"E147.trimOffspring");Q29=makeQuery(id+"F2.imprint","IMPRINT",FACE,{"disambiguationData":[TD([[makeQuery(id+"F2.imprint","IMPRINT",EDGE,{"derivedFrom":subQ0}),-1.0]])]});}
            var Q30;
            {var subQ0=sQuery(id+"F2.wireOp",EDGE,"E155.trimOffspring");Q30=makeQuery(id+"F2.imprint","IMPRINT",FACE,{"disambiguationData":[TD([[makeQuery(id+"F2.imprint","IMPRINT",EDGE,{"derivedFrom":subQ0}),1.0]])]});}
            var Q31;
            {var subQ0=sQuery(id+"F2.wireOp",EDGE,"E153.trimOffspring");Q31=makeQuery(id+"F2.imprint","IMPRINT",FACE,{"disambiguationData":[TD([[makeQuery(id+"F2.imprint","IMPRINT",EDGE,{"derivedFrom":subQ0}),1.0]])]});}
            var Q32;
            {var subQ0=sQuery(id+"F2.wireOp",EDGE,"E149.trimOffspring");Q32=makeQuery(id+"F2.imprint","IMPRINT",FACE,{"disambiguationData":[TD([[makeQuery(id+"F2.imprint","IMPRINT",EDGE,{"derivedFrom":subQ0}),-1.0]])]});}
            var Q33;
            {var subQ0=sQuery(id+"F2.wireOp",EDGE,"E132");Q33=makeQuery(id+"F2.imprint","IMPRINT",FACE,{"disambiguationData":[TD([[makeQuery(id+"F2.imprint","IMPRINT",EDGE,{"derivedFrom":subQ0}),-1.0]])]});}
            var Q34;
            Q34=makeQuery(id+"F2.imprint","IMPRINT",FACE,{"disambiguationData":[TD([[makeQuery(id+"F2.imprint","IMPRINT",EDGE,{"derivedFrom":sQuery(id+"F2.wireOp",EDGE,"0SM9cmPj-k588-dP9p-LpUl-VFwqECGHFw5M")}),1.0]])]});
            extrude(context, id + "F3", {"entities" : qUnion([Q0, Q1, Q2, Q3, Q4, Q5, Q6, Q7, Q8, Q9, Q10, Q11, Q12, Q13, Q14, Q15, Q16, Q17, Q18, Q19, Q20, Q21, Q22, Q23, Q24, Q25, Q26, Q27, Q28, Q29, Q30, Q31, Q32, Q33, Q34]), "operationType" : NewBodyOperationType.ADD, "depth" : 1.52 * mm});
        }
    });
